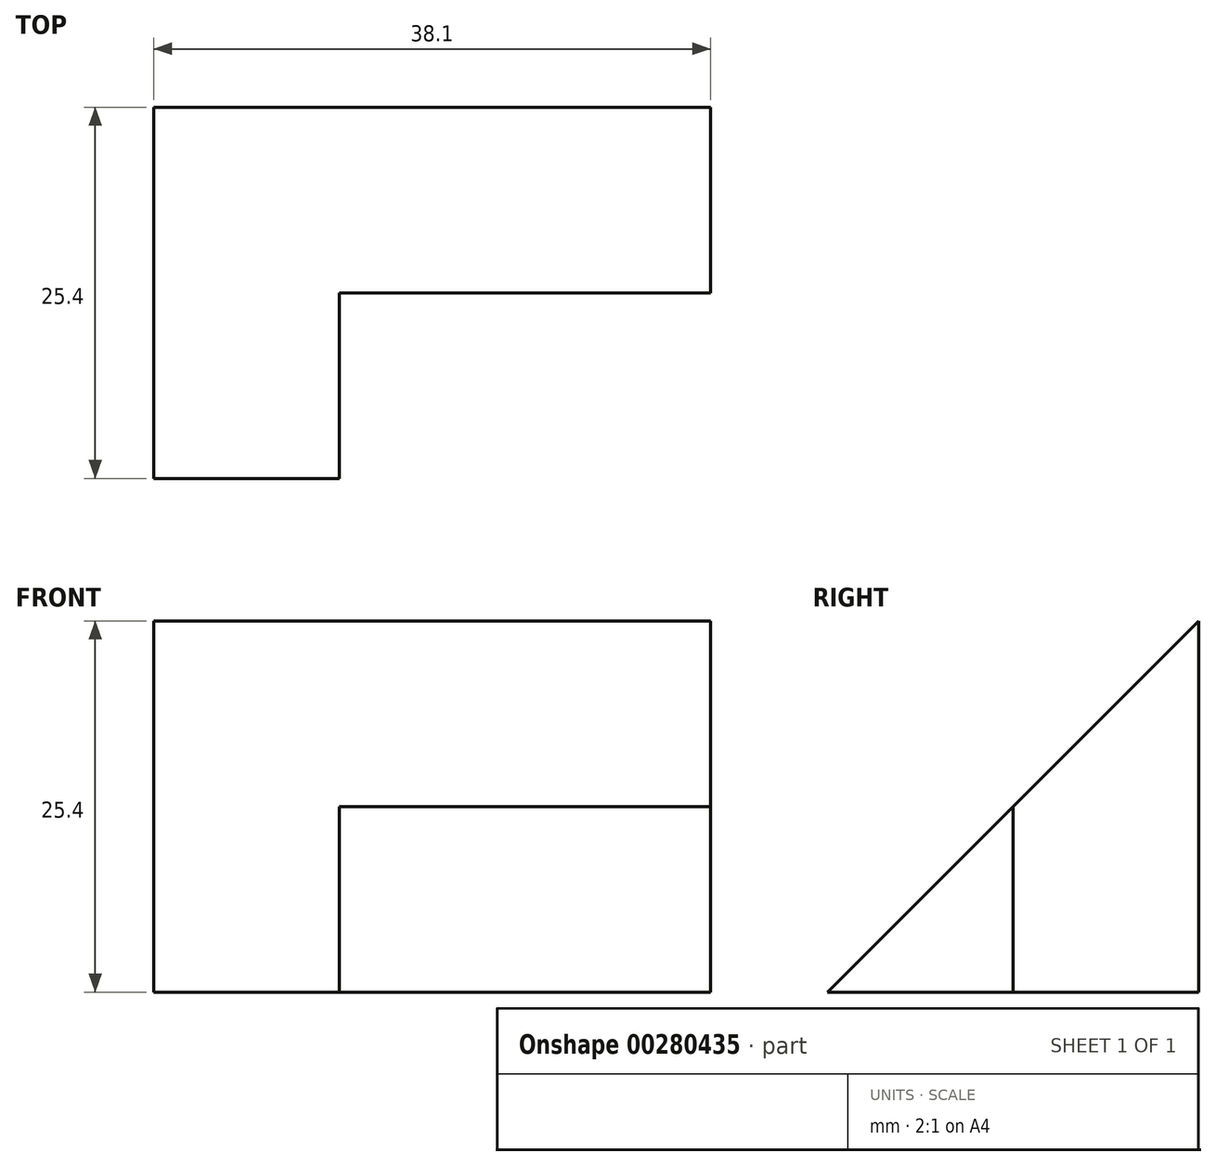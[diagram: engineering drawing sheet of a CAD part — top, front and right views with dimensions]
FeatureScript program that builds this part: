
annotation { "Feature Type Name" : "Feature", "Feature Type Description" : "" }
export const myFeature = defineFeature(function(context is Context, id is Id, definition is map)
    precondition{}
    {
        {
            var Q0;
            Q0=qCreatedBy(makeId("Front.planeOp"),FACE);
            var sketch = newSketch(context, id + "F0", { "sketchPlane" : qUnion([Q0])});
            skLineSegment(sketch, "E0", {"start": v(0, 0) * mm, "end": v(38.1, 0) * mm});
            skLineSegment(sketch, "E1", {"start": v(38.1, 0) * mm, "end": v(38.1, 25.4) * mm});
            skLineSegment(sketch, "E2", {"start": v(38.1, 25.4) * mm, "end": v(0, 25.4) * mm});
            skLineSegment(sketch, "E3", {"start": v(0, 25.4) * mm, "end": v(0, 0) * mm});
            skSolve(sketch);
        }
        {
            var Q0;
            Q0=qSketchRegion(id+"F0",true);
            extrude(context, id + "F1", {"entities" : qUnion([Q0]), "endBound" : BoundingType.SYMMETRIC, "depth" : 25.4 * mm});
        }
        {
            var Q0;
            Q0=makeQuery(id+"F1.opExtrude","SWEPT_FACE",FACE,{"disambiguationData":[OSD([sQuery(id+"F0.wireOp",EDGE,"E1")])]});
            var sketch = newSketch(context, id + "F2", { "sketchPlane" : qUnion([Q0])});
            skLineSegment(sketch, "E4", {"start": v(-12.7, 25.4) * mm, "end": v(-12.7, 0) * mm});
            skLineSegment(sketch, "E5", {"start": v(-12.7, 0) * mm, "end": v(12.7, 25.4) * mm});
            skLineSegment(sketch, "E6", {"start": v(12.7, 25.4) * mm, "end": v(-12.7, 25.4) * mm});
            skSolve(sketch);
        }
        {
            var Q0;
            Q0 = qSketchRegion(id + "F2", true);
            extrude(context, id + "F3", {"entities" : qUnion([Q0]), "operationType" : NewBodyOperationType.REMOVE, "endBound" : BoundingType.THROUGH_ALL, "oppositeDirection" : true, "depth" : 25.4 * mm});
        }
        {
            var Q0;
            Q0=makeQuery(id+"F1.opExtrude","SWEPT_FACE",FACE,{"disambiguationData":[OSD([sQuery(id+"F0.wireOp",EDGE,"E1")])]});
            var sketch = newSketch(context, id + "F4", { "sketchPlane" : qUnion([Q0])});
            skLineSegment(sketch, "E7", {"start": v(0, 12.7) * mm, "end": v(0, 0) * mm});
            skLineSegment(sketch, "E8", {"start": v(0, 0) * mm, "end": v(-12.7, 0) * mm});
            skLineSegment(sketch, "E9", {"start": v(-12.7, 0) * mm, "end": v(0, 12.7) * mm});
            skSolve(sketch);
        }
        {
            var Q0;
            Q0=makeQuery(id+"F4.imprint","IMPRINT",FACE,{"disambiguationData":[TD([[makeQuery(id+"F4.imprint","IMPRINT",EDGE,{"derivedFrom":sQuery(id+"F4.wireOp",EDGE,"E7")}),-1.0]])]});
            extrude(context, id + "F5", {"entities" : qUnion([Q0]), "operationType" : NewBodyOperationType.REMOVE, "oppositeDirection" : true, "depth" : 25.4 * mm});
        }
    });
